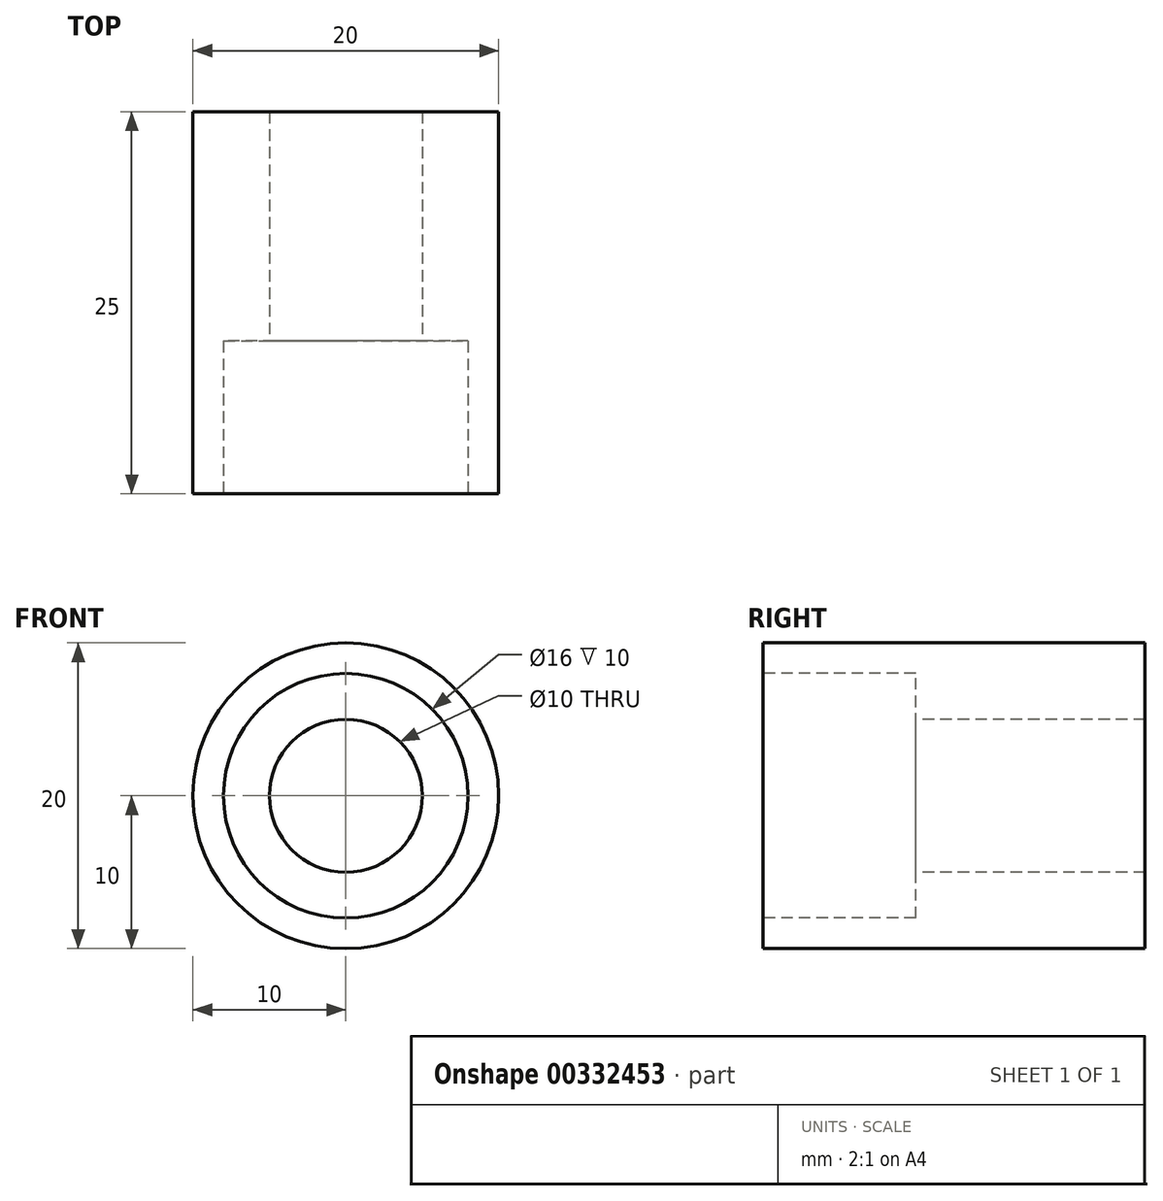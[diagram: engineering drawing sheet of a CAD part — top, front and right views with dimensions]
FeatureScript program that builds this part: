
annotation { "Feature Type Name" : "Feature", "Feature Type Description" : "" }
export const myFeature = defineFeature(function(context is Context, id is Id, definition is map)
    precondition{}
    {
        {
            var Q0;
            Q0=qCreatedBy(makeId("Front.planeOp"),FACE);
            var sketch = newSketch(context, id + "F0", { "sketchPlane" : qUnion([Q0])});
            skCircle(sketch, "E0", {"center": v(0, 0) * mm, "radius": 10 * mm});
            skSolve(sketch);
        }
        {
            var Q0;
            Q0 = qSketchRegion(id + "F0", true);
            extrude(context, id + "F1", {"entities" : qUnion([Q0]), "endBound" : BoundingType.SYMMETRIC, "depth" : 25 * mm});
        }
        {
            var Q0;
            Q0=qCreatedBy(makeId("Top.planeOp"),FACE);
            var sketch = newSketch(context, id + "F2", { "sketchPlane" : qUnion([Q0])});
            skLineSegment(sketch, "E1", {"start": v(0, 12.5) * mm, "end": v(0, -12.5) * mm});
            skLineSegment(sketch, "E2", {"start": v(0, -12.5) * mm, "end": v(8, -12.5) * mm});
            skLineSegment(sketch, "E3", {"start": v(8, -12.5) * mm, "end": v(8, -2.5) * mm});
            skLineSegment(sketch, "E4", {"start": v(8, -2.5) * mm, "end": v(5, -2.5) * mm});
            skLineSegment(sketch, "E5", {"start": v(5, -2.5) * mm, "end": v(5, 12.5) * mm});
            skLineSegment(sketch, "E6", {"start": v(5, 12.5) * mm, "end": v(0, 12.5) * mm});
            skLineSegment(sketch, "E7", {"start": v(0, 12.5) * mm, "end": v(0, 18) * mm, "construction": true});
            skSolve(sketch);
        }
        {
            var Q0;
            Q0 = qSketchRegion(id + "F2", true);
            var Q1;
            Q1=sQuery(id+"F2.wireOp",EDGE,"E7");
            revolve(context, id + "F3", {"operationType" : NewBodyOperationType.REMOVE, "entities" : qUnion([Q0]), "axis" : qUnion([Q1]), "revolveType" : RevolveType.FULL});
        }
    });
